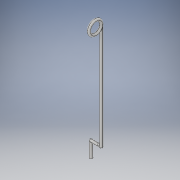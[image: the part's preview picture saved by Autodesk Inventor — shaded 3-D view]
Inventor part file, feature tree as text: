
AUTODESK INVENTOR PART (.ipt)
format: ipt  version: 2017 (Build 210142000, 142)  size: 168,960 bytes
history: native  units: in
note: dims shown in document units (in); Inventor stores cm internally (conversion verified against a paired STEP export)
features: extrude x2, sketch x2, fillet x1
ambient origin geometry x8: Origin, YZ Plane, XZ Plane, XY Plane, X Axis, Y Axis, Z Axis, Center Point
bodies: Solid1 (feature_tree)
feature tree (5):
  extrude  "Extrusion1"  Depth=0.034in
  extrude  "Extrusion3"  Depth=0.0165in
  fillet  "Fillet1"  Radius=0.034in
  sketch  "Sketch1"  dims[d0=0.034in d1=0.0in d4=0.154in]
  sketch  "Sketch2"  dims[d5=0.193in d6=1.262in d9=0.034in d10=0.034in d11=0.034in d12=0.11in d13=0.1in d14=0.0in d15=0.0165in]
